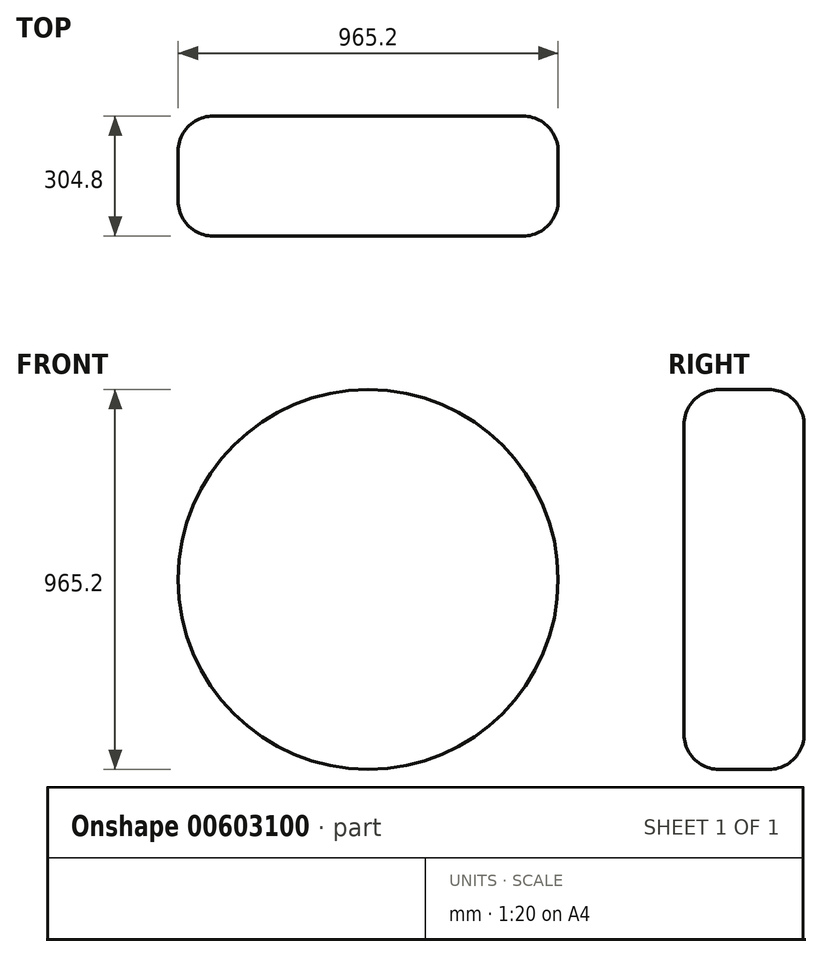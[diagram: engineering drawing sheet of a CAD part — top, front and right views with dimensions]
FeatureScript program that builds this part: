
annotation { "Feature Type Name" : "Feature", "Feature Type Description" : "" }
export const myFeature = defineFeature(function(context is Context, id is Id, definition is map)
    precondition{}
    {
        {
            var Q0;
            Q0=qCreatedBy(makeId("Front.planeOp"),FACE);
            var sketch = newSketch(context, id + "F0", { "sketchPlane" : qUnion([Q0])});
            skCircle(sketch, "E0", {"center": v(0, 0) * mm, "radius": 482.6 * mm});
            skSolve(sketch);
        }
        {
            var Q0;
            Q0 = qSketchRegion(id + "F0", true);
            extrude(context, id + "F1", {"entities" : qUnion([Q0]), "endBound" : BoundingType.SYMMETRIC, "depth" : 304.8 * mm, "offsetDistance" : 25.4 * mm});
        }
        {
            var Q0;
            Q0=makeQuery(id+"F1.opExtrude","CAP_EDGE",EDGE,{"disambiguationData":[OSD([sQuery(id+"F0.wireOp",EDGE,"E0")])],"isStart":false});
            var Q1;
            Q1=makeQuery(id+"F1.opExtrude","CAP_EDGE",EDGE,{"disambiguationData":[OSD([sQuery(id+"F0.wireOp",EDGE,"E0")])],"isStart":true});
            fillet(context, id + "F2", {"entities" : qUnion([Q0, Q1]), "radius" : 88.9 * mm, "tangentPropagation" : true, "allowEdgeOverflow" : false});
        }
    });
